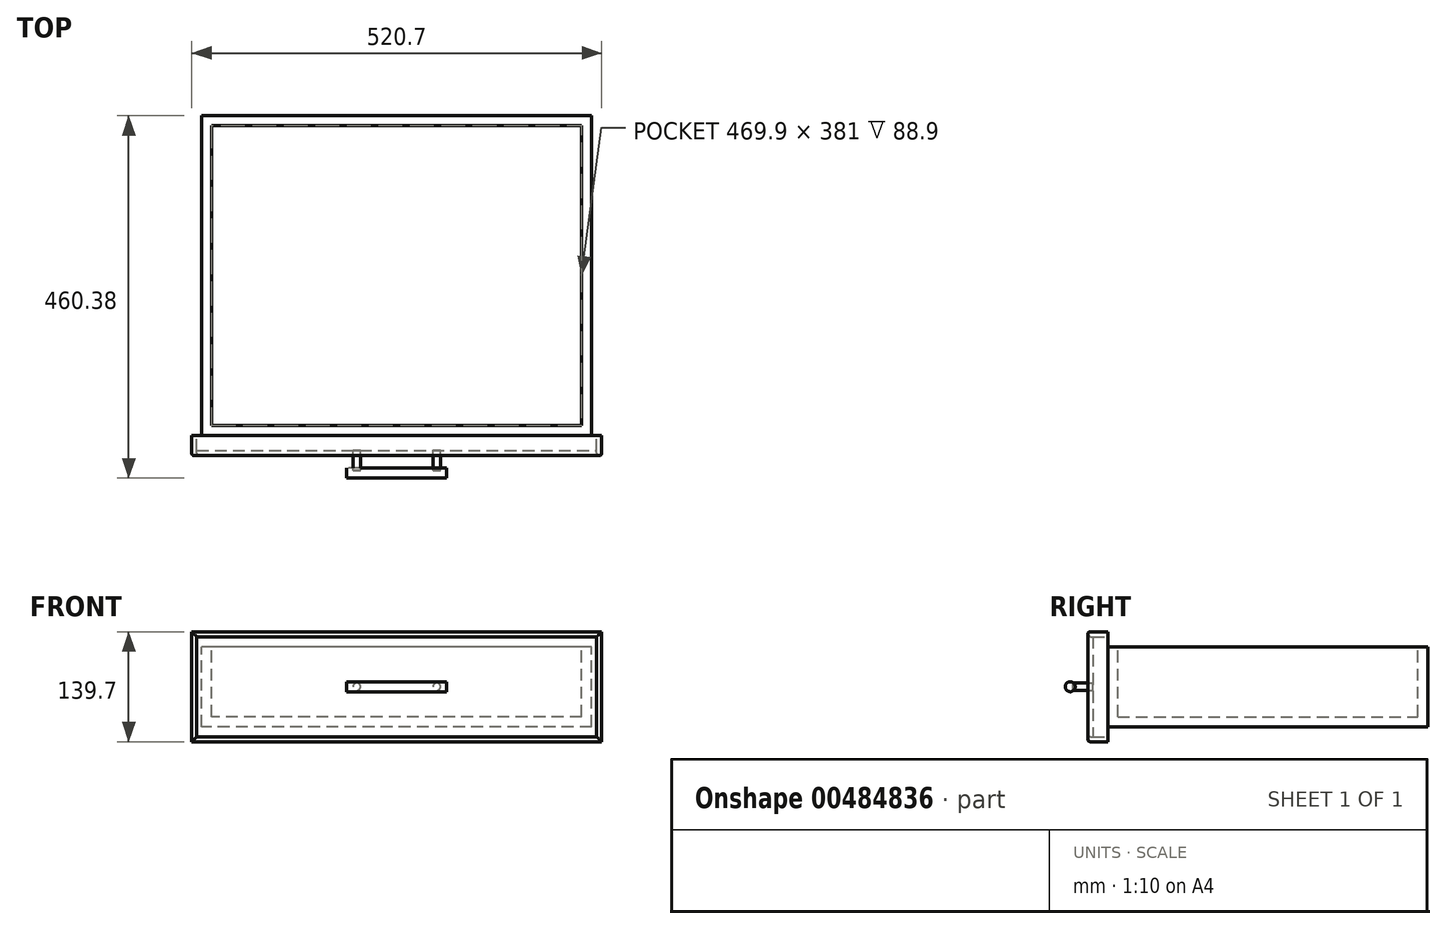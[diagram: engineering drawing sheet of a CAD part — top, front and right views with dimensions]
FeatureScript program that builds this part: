
annotation { "Feature Type Name" : "Feature", "Feature Type Description" : "" }
export const myFeature = defineFeature(function(context is Context, id is Id, definition is map)
    precondition{}
    {
        {
            var Q0;
            Q0=qCreatedBy(makeId("Front.planeOp"),FACE);
            var sketch = newSketch(context, id + "F0", { "sketchPlane" : qUnion([Q0])});
            skLineSegment(sketch, "E0.bottom", {"start": v(247.65, 50.8) * mm, "end": v(-247.65, 50.8) * mm});
            skLineSegment(sketch, "E0.top", {"start": v(247.65, -50.8) * mm, "end": v(-247.65, -50.8) * mm});
            skLineSegment(sketch, "E0.left", {"start": v(-247.65, -50.8) * mm, "end": v(-247.65, 50.8) * mm});
            skLineSegment(sketch, "E0.right", {"start": v(247.65, -50.8) * mm, "end": v(247.65, 50.8) * mm});
            skSolve(sketch);
        }
        {
            var Q0;
            Q0 = qSketchRegion(id + "F0", true);
            extrude(context, id + "F1", {"entities" : qUnion([Q0]), "depth" : 406.4 * mm, "offsetDistance" : 25.4 * mm});
        }
        {
            var Q0;
            Q0=makeQuery(id+"F1.opExtrude","SWEPT_FACE",FACE,{"disambiguationData":[OSD([sQuery(id+"F0.wireOp",EDGE,"E0.bottom")])]});
            shell(context, id + "F2", {"entities" : qUnion([Q0]), "thickness" : 12.7 * mm});
        }
        {
            var Q0;
            Q0=makeQuery(id+"F1.opExtrude","CAP_FACE",FACE,{"disambiguationData":[OSD([sQuery(id+"F0.wireOp",EDGE,"E0.bottom"),sQuery(id+"F0.wireOp",EDGE,"E0.top"),sQuery(id+"F0.wireOp",EDGE,"E0.left"),sQuery(id+"F0.wireOp",EDGE,"E0.right")])],"isStart":false});
            var sketch = newSketch(context, id + "F3", { "sketchPlane" : qUnion([Q0])});
            skLineSegment(sketch, "E1.bottom", {"start": v(-254, 63.5) * mm, "end": v(254, 63.5) * mm});
            skLineSegment(sketch, "E1.top", {"start": v(-254, -63.5) * mm, "end": v(254, -63.5) * mm});
            skLineSegment(sketch, "E1.left", {"start": v(-254, 63.5) * mm, "end": v(-254, -63.5) * mm});
            skLineSegment(sketch, "E1.right", {"start": v(254, 63.5) * mm, "end": v(254, -63.5) * mm});
            skPoint(sketch, "E1.middle", {"position": v(0, 0) * mm});
            skSolve(sketch);
        }
        {
            var Q0;
            Q0 = qSketchRegion(id + "F3", true);
            extrude(context, id + "F4", {"entities" : qUnion([Q0]), "depth" : 19.05 * mm, "offsetDistance" : 25.4 * mm});
        }
        {
            var Q0;
            Q0=makeQuery(id+"F4.opExtrude","CAP_FACE",FACE,{"disambiguationData":[OSD([sQuery(id+"F3.wireOp",EDGE,"E1.bottom"),sQuery(id+"F3.wireOp",EDGE,"E1.top"),sQuery(id+"F3.wireOp",EDGE,"E1.left"),sQuery(id+"F3.wireOp",EDGE,"E1.right")])],"isStart":true});
            var sketch = newSketch(context, id + "F5", { "sketchPlane" : qUnion([Q0])});
            skLineSegment(sketch, "E2.bottom", {"start": v(254, 63.5) * mm, "end": v(-254, 63.5) * mm});
            skLineSegment(sketch, "E2.top", {"start": v(254, -63.5) * mm, "end": v(-254, -63.5) * mm});
            skLineSegment(sketch, "E2.left", {"start": v(254, 63.5) * mm, "end": v(254, -63.5) * mm});
            skLineSegment(sketch, "E2.right", {"start": v(-254, 63.5) * mm, "end": v(-254, -63.5) * mm});
            skPoint(sketch, "E2.middle", {"position": v(0, 0) * mm});
            skLineSegment(sketch, "E3.bottom", {"start": v(-260.35, 69.85) * mm, "end": v(260.35, 69.85) * mm});
            skLineSegment(sketch, "E3.top", {"start": v(-260.35, -69.85) * mm, "end": v(260.35, -69.85) * mm});
            skLineSegment(sketch, "E3.left", {"start": v(-260.35, 69.85) * mm, "end": v(-260.35, -69.85) * mm});
            skLineSegment(sketch, "E3.right", {"start": v(260.35, 69.85) * mm, "end": v(260.35, -69.85) * mm});
            skLineSegment(sketch, "E4", {"start": v(254, 63.5) * mm, "end": v(260.35, 69.85) * mm});
            skLineSegment(sketch, "E5", {"start": v(-254, 63.5) * mm, "end": v(-260.35, 69.85) * mm});
            skLineSegment(sketch, "E6", {"start": v(-254, -63.5) * mm, "end": v(-260.35, -69.85) * mm});
            skLineSegment(sketch, "E7", {"start": v(254, -63.5) * mm, "end": v(260.35, -69.85) * mm});
            skSolve(sketch);
        }
        {
            var Q0;
            Q0 = qSketchRegion(id + "F5", true);
            extrude(context, id + "F6", {"entities" : qUnion([Q0]), "oppositeDirection" : true, "depth" : 25.4 * mm, "offsetDistance" : 25.4 * mm});
        }
        {
            var Q0;
            Q0=makeQuery(id+"F6.opExtrude","CAP_EDGE",EDGE,{"disambiguationData":[OSD([sQuery(id+"F5.wireOp",EDGE,"E3.bottom")])],"isStart":false});
            var Q1;
            Q1=makeQuery(id+"F6.opExtrude","CAP_EDGE",EDGE,{"disambiguationData":[OSD([sQuery(id+"F5.wireOp",EDGE,"E3.right")])],"isStart":false});
            var Q2;
            Q2=makeQuery(id+"F6.opExtrude","CAP_EDGE",EDGE,{"disambiguationData":[OSD([sQuery(id+"F5.wireOp",EDGE,"E3.left")])],"isStart":false});
            var Q3;
            Q3=makeQuery(id+"F6.opExtrude","CAP_EDGE",EDGE,{"disambiguationData":[OSD([sQuery(id+"F5.wireOp",EDGE,"E3.top")])],"isStart":false});
            var Q4;
            Q4=makeQuery(id+"F6.opExtrude","CAP_EDGE",EDGE,{"disambiguationData":[OSD([sQuery(id+"F5.wireOp",EDGE,"E2.top")])],"isStart":false});
            var Q5;
            Q5=makeQuery(id+"F6.opExtrude","CAP_EDGE",EDGE,{"disambiguationData":[OSD([sQuery(id+"F5.wireOp",EDGE,"E2.right")])],"isStart":false});
            var Q6;
            Q6=makeQuery(id+"F6.opExtrude","CAP_EDGE",EDGE,{"disambiguationData":[OSD([sQuery(id+"F5.wireOp",EDGE,"E2.left")])],"isStart":false});
            var Q7;
            Q7=makeQuery(id+"F6.opExtrude","CAP_EDGE",EDGE,{"disambiguationData":[OSD([sQuery(id+"F5.wireOp",EDGE,"E2.bottom")])],"isStart":false});
            fillet(context, id + "F7", {"entities" : qUnion([Q0, Q1, Q2, Q3, Q4, Q5, Q6, Q7]), "radius" : 3.17 * mm, "tangentPropagation" : true, "allowEdgeOverflow" : false});
        }
        {
            var Q0;
            Q0=makeQuery(id+"F4.opExtrude","CAP_FACE",FACE,{"disambiguationData":[OSD([sQuery(id+"F3.wireOp",EDGE,"E1.bottom"),sQuery(id+"F3.wireOp",EDGE,"E1.top"),sQuery(id+"F3.wireOp",EDGE,"E1.left"),sQuery(id+"F3.wireOp",EDGE,"E1.right")])],"isStart":false});
            var sketch = newSketch(context, id + "F8", { "sketchPlane" : qUnion([Q0])});
            skLineSegment(sketch, "E8", {"start": v(0, 0) * mm, "end": v(-50.8, 0) * mm});
            skLineSegment(sketch, "E9", {"start": v(-50.8, 0) * mm, "end": v(50.8, 0) * mm});
            skCircle(sketch, "E10", {"center": v(-50.8, 0) * mm, "radius": 4.76 * mm});
            skCircle(sketch, "E11", {"center": v(50.8, 0) * mm, "radius": 4.76 * mm});
            skSolve(sketch);
        }
        {
            var Q0;
            Q0 = qSketchRegion(id + "F8", true);
            extrude(context, id + "F9", {"entities" : qUnion([Q0]), "depth" : 25.4 * mm, "offsetDistance" : 25.4 * mm});
        }
        {
            var Q0;
            Q0=qCreatedBy(makeId("Right.planeOp"),FACE);
            var sketch = newSketch(context, id + "F10", { "sketchPlane" : qUnion([Q0])});
            skCircle(sketch, "E12", {"center": v(-454.03, 0) * mm, "radius": 6.35 * mm});
            skSolve(sketch);
        }
        {
            var Q0;
            Q0 = qSketchRegion(id + "F10", true);
            extrude(context, id + "F11", {"entities" : qUnion([Q0]), "endBound" : BoundingType.SYMMETRIC, "depth" : 127 * mm, "offsetDistance" : 25.4 * mm});
        }
    });
